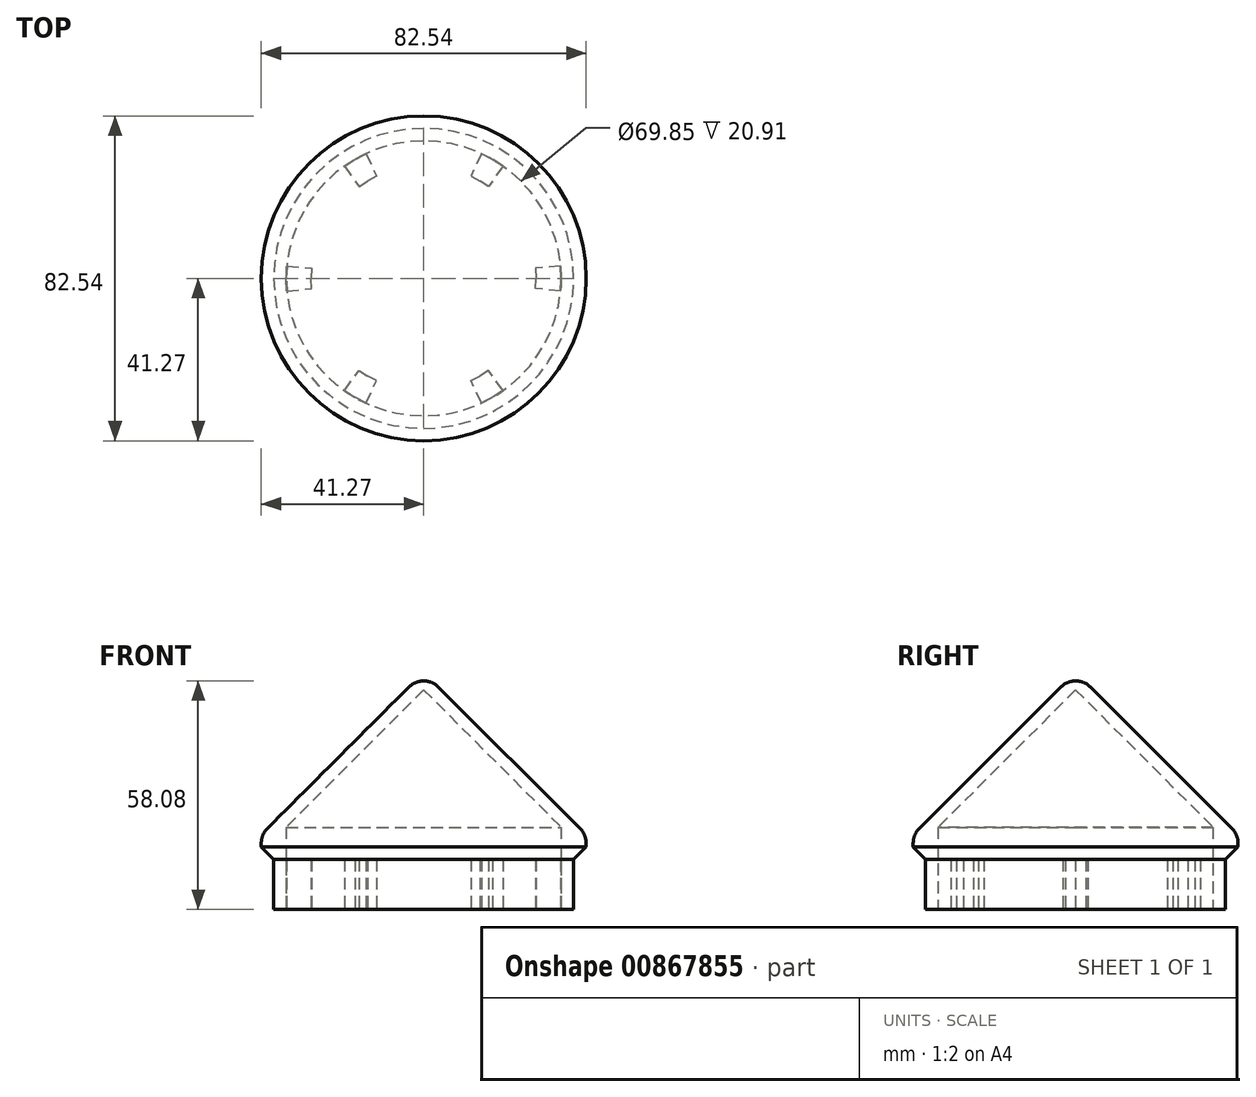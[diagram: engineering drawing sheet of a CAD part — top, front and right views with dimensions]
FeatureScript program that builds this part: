
annotation { "Feature Type Name" : "Feature", "Feature Type Description" : "" }
export const myFeature = defineFeature(function(context is Context, id is Id, definition is map)
    precondition{}
    {
        {
            var Q0;
            Q0=qCreatedBy(makeId("Front.planeOp"),FACE);
            var sketch = newSketch(context, id + "F0", { "sketchPlane" : qUnion([Q0])});
            skLineSegment(sketch, "E0", {"start": v(0, 0) * mm, "end": v(-6.35, 0) * mm});
            skLineSegment(sketch, "E1", {"start": v(-34.92, 0) * mm, "end": v(-38.1, 0) * mm});
            skLineSegment(sketch, "E2", {"start": v(-38.1, 0) * mm, "end": v(-38.1, 12.7) * mm});
            skLineSegment(sketch, "E3", {"start": v(-38.1, 12.7) * mm, "end": v(-41.27, 15.88) * mm});
            skLineSegment(sketch, "E4", {"start": v(0, 0) * mm, "end": v(-4.76, 0) * mm});
            skLineSegment(sketch, "E5", {"start": v(-4.76, 0) * mm, "end": v(-6.35, 0) * mm});
            skLineSegment(sketch, "E6", {"start": v(-6.35, 0) * mm, "end": v(-6.35, 3.18) * mm});
            skLineSegment(sketch, "E7", {"start": v(-6.35, 3.18) * mm, "end": v(-7.11, 6.35) * mm});
            skLineSegment(sketch, "E8", {"start": v(-7.11, 6.35) * mm, "end": v(-6.35, 6.35) * mm});
            skLineSegment(sketch, "E9", {"start": v(-6.35, 6.35) * mm, "end": v(-6.35, 8.38) * mm});
            skLineSegment(sketch, "E10", {"start": v(-6.35, 8.38) * mm, "end": v(-7.11, 11.56) * mm});
            skLineSegment(sketch, "E11", {"start": v(-7.11, 11.56) * mm, "end": v(-6.35, 11.56) * mm});
            skLineSegment(sketch, "E12", {"start": v(-6.35, 11.56) * mm, "end": v(-6.35, 13.59) * mm});
            skLineSegment(sketch, "E13", {"start": v(-6.35, 13.59) * mm, "end": v(-7.11, 16.76) * mm});
            skLineSegment(sketch, "E14", {"start": v(-7.11, 16.76) * mm, "end": v(-6.35, 16.76) * mm});
            skLineSegment(sketch, "E15", {"start": v(-6.35, 16.76) * mm, "end": v(-6.35, 18.8) * mm});
            skLineSegment(sketch, "E16", {"start": v(-6.35, 18.8) * mm, "end": v(-7.11, 21.97) * mm});
            skLineSegment(sketch, "E17", {"start": v(-7.11, 21.97) * mm, "end": v(-6.35, 21.97) * mm});
            skPoint(sketch, "E18.orphan", {"position": v(-7.11, 0) * mm});
            skLineSegment(sketch, "E19", {"start": v(-6.35, 0) * mm, "end": v(-7.11, 0) * mm});
            skLineSegment(sketch, "E20", {"start": v(-25.4, 0) * mm, "end": v(-28.58, 0) * mm});
            skLineSegment(sketch, "E21", {"start": v(-28.58, 0) * mm, "end": v(-34.92, 0) * mm});
            skLineSegment(sketch, "E22", {"start": v(-28.57, 0) * mm, "end": v(-28.57, 12.7) * mm});
            skLineSegment(sketch, "E23", {"start": v(-25.4, 0) * mm, "end": v(-25.4, 11.11) * mm});
            skLineSegment(sketch, "E24", {"start": v(-25.4, 11.11) * mm, "end": v(-6.35, 32.41) * mm});
            skLineSegment(sketch, "E25", {"start": v(-6.35, 32.41) * mm, "end": v(-6.35, 21.97) * mm});
            skLineSegment(sketch, "E26", {"start": v(-28.57, 12.7) * mm, "end": v(-8.9, 34.7) * mm});
            skLineSegment(sketch, "E27", {"start": v(-25.4, 0) * mm, "end": v(-6.35, 0) * mm, "construction": true});
            skLineSegment(sketch, "E28", {"start": v(-4.76, 0) * mm, "end": v(-4.76, 34.7) * mm});
            skLineSegment(sketch, "E29", {"start": v(-4.76, 34.7) * mm, "end": v(-8.9, 34.7) * mm});
            skLineSegment(sketch, "E30", {"start": v(-6.35, 32.41) * mm, "end": v(-8.9, 34.7) * mm, "construction": true});
            skLineSegment(sketch, "E31", {"start": v(-41.27, 15.88) * mm, "end": v(-41.27, 19.06) * mm});
            skLineSegment(sketch, "E32", {"start": v(-34.92, 0) * mm, "end": v(-34.92, 20.92) * mm});
            skLineSegment(sketch, "E33", {"start": v(-34.92, 20.92) * mm, "end": v(0, 55.84) * mm});
            skLineSegment(sketch, "E34", {"start": v(0, 0) * mm, "end": v(0, 55.84) * mm, "construction": true});
            skLineSegment(sketch, "E35", {"start": v(-41.27, 19.06) * mm, "end": v(-2.25, 58.09) * mm});
            skLineSegment(sketch, "E36", {"start": v(0, 58.09) * mm, "end": v(-2.25, 58.09) * mm});
            skLineSegment(sketch, "E37", {"start": v(0, 55.84) * mm, "end": v(0, 58.09) * mm});
            skSolve(sketch);
        }
        {
            var Q0;
            Q0=makeQuery(id+"F0.imprint","IMPRINT",FACE,{"disambiguationData":[TD([[makeQuery(id+"F0.imprint","IMPRINT",EDGE,{"derivedFrom":sQuery(id+"F0.wireOp",EDGE,"E1")}),-1.0]])]});
            var Q1;
            Q1=makeQuery(id+"F0.imprint","IMPRINT",FACE,{"disambiguationData":[TD([[makeQuery(id+"F0.imprint","IMPRINT",EDGE,{"derivedFrom":sQuery(id+"F0.wireOp",EDGE,"E5")}),-1.0]])]});
            var Q2;
            Q2=sQuery(id+"F0.wireOp",EDGE,"E34");
            revolve(context, id + "F1", {"surfaceOperationType" : NewSurfaceOperationType.NEW, "entities" : qUnion([Q0, Q1]), "axis" : qUnion([Q2]), "revolveType" : RevolveType.FULL});
        }
        {
            var Q0;
            Q0=makeQuery(id+"F1.opRevolve","SWEPT_FACE",FACE,{"disambiguationData":[OSD([sQuery(id+"F0.wireOp",EDGE,"E1")])]});
            var sketch = newSketch(context, id + "F2", { "sketchPlane" : qUnion([Q0])});
            skLineSegment(sketch, "E38", {"start": v(-34.78, -3.17) * mm, "end": v(-28.46, -2.6) * mm});
            skLineSegment(sketch, "E39", {"start": v(-28.46, -2.6) * mm, "end": v(-28.57, 0) * mm});
            skLineSegment(sketch, "E40", {"start": v(-34.78, 3.17) * mm, "end": v(-28.46, 2.6) * mm});
            skLineSegment(sketch, "E41", {"start": v(-28.46, 2.6) * mm, "end": v(-28.57, 0) * mm});
            skLineSegment(sketch, "E42", {"start": v(0, 0) * mm, "end": v(-28.57, 0) * mm, "construction": true});
            skLineSegment(sketch, "E43", {"start": v(0, 0) * mm, "end": v(0, 11.7) * mm, "construction": true});
            skLineSegment(sketch, "E44", {"start": v(-28.57, 0) * mm, "end": v(-34.92, 0) * mm, "construction": true});
            skLineSegment(sketch, "E45", {"start": v(-34.78, -3.17) * mm, "end": v(-34.92, 0) * mm});
            skLineSegment(sketch, "E46", {"start": v(-34.78, 3.17) * mm, "end": v(-34.92, 0) * mm});
            skLineSegment(sketch, "E47.1.0", {"start": v(-20.14, -28.54) * mm, "end": v(-16.48, -23.35) * mm});
            skLineSegment(sketch, "E47.1.1", {"start": v(-20.14, -28.54) * mm, "end": v(-17.46, -30.25) * mm});
            skLineSegment(sketch, "E47.1.2", {"start": v(-14.64, -31.7) * mm, "end": v(-17.46, -30.25) * mm});
            skLineSegment(sketch, "E47.1.3", {"start": v(-14.64, -31.7) * mm, "end": v(-11.98, -25.94) * mm});
            skLineSegment(sketch, "E47.1.4", {"start": v(-11.98, -25.94) * mm, "end": v(-14.29, -24.75) * mm});
            skLineSegment(sketch, "E47.1.5", {"start": v(-16.48, -23.35) * mm, "end": v(-14.29, -24.75) * mm});
            skLineSegment(sketch, "E47.2.0", {"start": v(14.64, -31.7) * mm, "end": v(11.98, -25.94) * mm});
            skLineSegment(sketch, "E47.2.1", {"start": v(14.64, -31.7) * mm, "end": v(17.46, -30.25) * mm});
            skLineSegment(sketch, "E47.2.2", {"start": v(20.14, -28.54) * mm, "end": v(17.46, -30.25) * mm});
            skLineSegment(sketch, "E47.2.3", {"start": v(20.14, -28.54) * mm, "end": v(16.48, -23.35) * mm});
            skLineSegment(sketch, "E47.2.4", {"start": v(16.48, -23.35) * mm, "end": v(14.29, -24.75) * mm});
            skLineSegment(sketch, "E47.2.5", {"start": v(11.98, -25.94) * mm, "end": v(14.29, -24.75) * mm});
            skLineSegment(sketch, "E47.3.0", {"start": v(34.78, -3.17) * mm, "end": v(28.46, -2.6) * mm});
            skLineSegment(sketch, "E47.3.1", {"start": v(34.78, -3.17) * mm, "end": v(34.92, 0) * mm});
            skLineSegment(sketch, "E47.3.2", {"start": v(34.78, 3.17) * mm, "end": v(34.92, 0) * mm});
            skLineSegment(sketch, "E47.3.3", {"start": v(34.78, 3.17) * mm, "end": v(28.46, 2.6) * mm});
            skLineSegment(sketch, "E47.3.4", {"start": v(28.46, 2.6) * mm, "end": v(28.57, 0) * mm});
            skLineSegment(sketch, "E47.3.5", {"start": v(28.46, -2.6) * mm, "end": v(28.57, 0) * mm});
            skLineSegment(sketch, "E47.4.0", {"start": v(20.14, 28.54) * mm, "end": v(16.48, 23.35) * mm});
            skLineSegment(sketch, "E47.4.1", {"start": v(20.14, 28.54) * mm, "end": v(17.46, 30.25) * mm});
            skLineSegment(sketch, "E47.4.2", {"start": v(14.64, 31.7) * mm, "end": v(17.46, 30.25) * mm});
            skLineSegment(sketch, "E47.4.3", {"start": v(14.64, 31.7) * mm, "end": v(11.98, 25.94) * mm});
            skLineSegment(sketch, "E47.4.4", {"start": v(11.98, 25.94) * mm, "end": v(14.29, 24.75) * mm});
            skLineSegment(sketch, "E47.4.5", {"start": v(16.48, 23.35) * mm, "end": v(14.29, 24.75) * mm});
            skLineSegment(sketch, "E47.5.0", {"start": v(-14.64, 31.7) * mm, "end": v(-11.98, 25.94) * mm});
            skLineSegment(sketch, "E47.5.1", {"start": v(-14.64, 31.7) * mm, "end": v(-17.46, 30.25) * mm});
            skLineSegment(sketch, "E47.5.2", {"start": v(-20.14, 28.54) * mm, "end": v(-17.46, 30.25) * mm});
            skLineSegment(sketch, "E47.5.3", {"start": v(-20.14, 28.54) * mm, "end": v(-16.48, 23.35) * mm});
            skLineSegment(sketch, "E47.5.4", {"start": v(-16.48, 23.35) * mm, "end": v(-14.29, 24.75) * mm});
            skLineSegment(sketch, "E47.5.5", {"start": v(-11.98, 25.94) * mm, "end": v(-14.29, 24.75) * mm});
            skPoint(sketch, "E47.center", {"position": v(0, 0) * mm});
            skSolve(sketch);
        }
        {
            var Q0;
            Q0=makeQuery(id+"F2.imprint","IMPRINT",FACE,{"disambiguationData":[TD([[makeQuery(id+"F2.imprint","IMPRINT",EDGE,{"derivedFrom":sQuery(id+"F2.wireOp",EDGE,"E38")}),1.0]])]});
            var Q1;
            Q1=makeQuery(id+"F2.imprint","IMPRINT",FACE,{"disambiguationData":[TD([[makeQuery(id+"F2.imprint","IMPRINT",EDGE,{"derivedFrom":sQuery(id+"F2.wireOp",EDGE,"E47.5.0")}),-1.0]])]});
            var Q2;
            Q2=makeQuery(id+"F2.imprint","IMPRINT",FACE,{"disambiguationData":[TD([[makeQuery(id+"F2.imprint","IMPRINT",EDGE,{"derivedFrom":sQuery(id+"F2.wireOp",EDGE,"E47.4.0")}),-1.0]])]});
            var Q3;
            Q3=makeQuery(id+"F2.imprint","IMPRINT",FACE,{"disambiguationData":[TD([[makeQuery(id+"F2.imprint","IMPRINT",EDGE,{"derivedFrom":sQuery(id+"F2.wireOp",EDGE,"E47.3.0")}),-1.0]])]});
            var Q4;
            Q4=makeQuery(id+"F2.imprint","IMPRINT",FACE,{"disambiguationData":[TD([[makeQuery(id+"F2.imprint","IMPRINT",EDGE,{"derivedFrom":sQuery(id+"F2.wireOp",EDGE,"E47.2.0")}),-1.0]])]});
            var Q5;
            Q5=makeQuery(id+"F2.imprint","IMPRINT",FACE,{"disambiguationData":[TD([[makeQuery(id+"F2.imprint","IMPRINT",EDGE,{"derivedFrom":sQuery(id+"F2.wireOp",EDGE,"E47.1.0")}),-1.0]])]});
            extrude(context, id + "F3", {"entities" : qUnion([Q0, Q1, Q2, Q3, Q4, Q5]), "operationType" : NewBodyOperationType.ADD, "oppositeDirection" : true, "depth" : 12.7 * mm, "offsetDistance" : 25.4 * mm});
        }
        {
            var Q0;
            Q0=makeQuery(id+"F1.opRevolve","SWEPT_FACE",FACE,{"disambiguationData":[OSD([sQuery(id+"F0.wireOp",EDGE,"E35")])]});
            fillet(context, id + "F4", {"entities" : qUnion([Q0]), "radius" : 5.42 * mm, "tangentPropagation" : true, "allowEdgeOverflow" : false});
        }
    });
